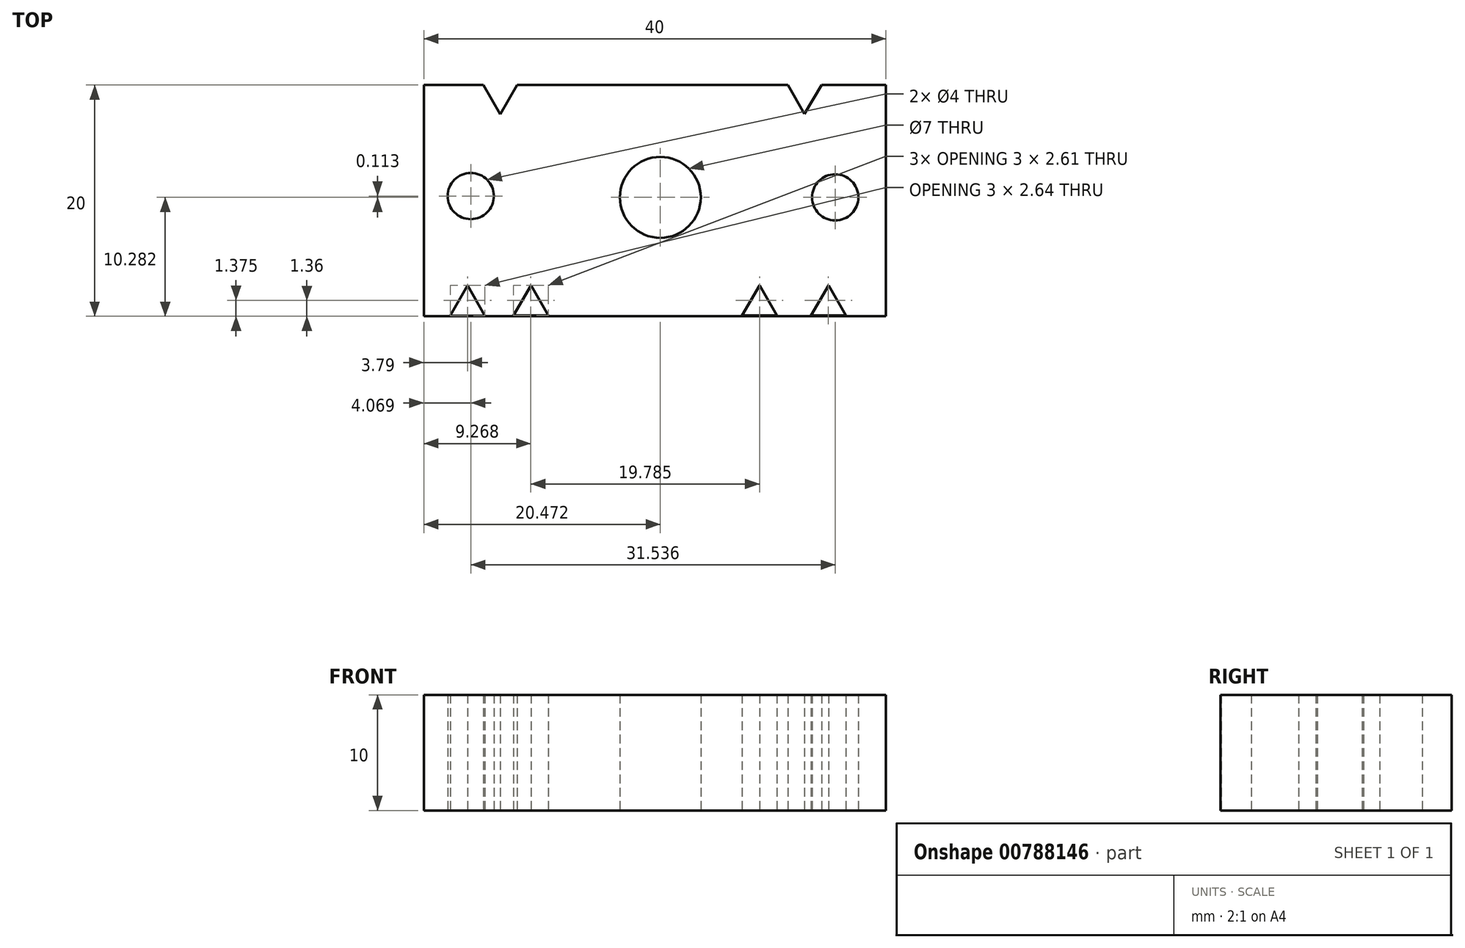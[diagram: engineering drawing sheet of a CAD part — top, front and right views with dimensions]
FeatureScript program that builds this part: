
annotation { "Feature Type Name" : "Feature", "Feature Type Description" : "" }
export const myFeature = defineFeature(function(context is Context, id is Id, definition is map)
    precondition{}
    {
        {
            var Q0;
            Q0=qCreatedBy(makeId("Top.planeOp"),FACE);
            var sketch = newSketch(context, id + "F0", { "sketchPlane" : qUnion([Q0])});
            skLineSegment(sketch, "E0.bottom", {"start": v(-22.8, 21.37) * mm, "end": v(17.2, 21.37) * mm});
            skLineSegment(sketch, "E0.top", {"start": v(-22.8, 1.37) * mm, "end": v(17.2, 1.37) * mm});
            skLineSegment(sketch, "E0.left", {"start": v(-22.8, 21.37) * mm, "end": v(-22.8, 1.37) * mm});
            skLineSegment(sketch, "E0.right", {"start": v(17.2, 21.37) * mm, "end": v(17.2, 1.37) * mm});
            skSolve(sketch);
        }
        {
            var Q0;
            Q0=makeQuery(id+"F0.imprint","IMPRINT",FACE,{"disambiguationData":[TD([[makeQuery(id+"F0.imprint","IMPRINT",EDGE,{"derivedFrom":sQuery(id+"F0.wireOp",EDGE,"E0.bottom")}),-1.0]])]});
            var sketch = newSketch(context, id + "F1", { "sketchPlane" : qUnion([Q0])});
            skLineSegment(sketch, "E1", {"start": v(-20.5, 1.44) * mm, "end": v(-19, 4.05) * mm});
            skLineSegment(sketch, "E2", {"start": v(-19, 4.05) * mm, "end": v(-17.5, 1.4) * mm});
            skLineSegment(sketch, "E3", {"start": v(-17.5, 1.4) * mm, "end": v(-20.5, 1.44) * mm});
            skLineSegment(sketch, "E4", {"start": v(-15.03, 1.44) * mm, "end": v(-13.5, 4.05) * mm});
            skLineSegment(sketch, "E5", {"start": v(-13.5, 4.05) * mm, "end": v(-12.03, 1.44) * mm});
            skLineSegment(sketch, "E6", {"start": v(-12.03, 1.44) * mm, "end": v(-15.03, 1.44) * mm});
            skLineSegment(sketch, "E7", {"start": v(4.75, 1.44) * mm, "end": v(6.28, 4.05) * mm});
            skLineSegment(sketch, "E8", {"start": v(6.28, 4.05) * mm, "end": v(7.75, 1.44) * mm});
            skLineSegment(sketch, "E9", {"start": v(7.75, 1.44) * mm, "end": v(4.75, 1.44) * mm});
            skLineSegment(sketch, "E10", {"start": v(10.72, 1.44) * mm, "end": v(12.24, 4.05) * mm});
            skLineSegment(sketch, "E11", {"start": v(12.24, 4.05) * mm, "end": v(13.72, 1.44) * mm});
            skLineSegment(sketch, "E12", {"start": v(13.72, 1.44) * mm, "end": v(10.72, 1.44) * mm});
            skLineSegment(sketch, "E13", {"start": v(-14.68, 21.44) * mm, "end": v(-17.68, 21.44) * mm});
            skLineSegment(sketch, "E14", {"start": v(-17.68, 21.44) * mm, "end": v(-16.18, 18.84) * mm});
            skLineSegment(sketch, "E15", {"start": v(-16.18, 18.84) * mm, "end": v(-14.68, 21.44) * mm});
            skLineSegment(sketch, "E16", {"start": v(11.65, 21.44) * mm, "end": v(8.65, 21.47) * mm});
            skLineSegment(sketch, "E17", {"start": v(8.65, 21.47) * mm, "end": v(10.13, 18.85) * mm});
            skLineSegment(sketch, "E18", {"start": v(10.13, 18.85) * mm, "end": v(11.65, 21.44) * mm});
            skCircle(sketch, "E19", {"center": v(-18.73, 11.76) * mm, "radius": 2 * mm});
            skCircle(sketch, "E20", {"center": v(12.8, 11.65) * mm, "radius": 2 * mm});
            skCircle(sketch, "E21", {"center": v(-2.33, 11.65) * mm, "radius": 3.5 * mm});
            skSolve(sketch);
        }
        {
            var Q0;
            Q0=makeQuery(id+"F0.imprint","IMPRINT",FACE,{"disambiguationData":[TD([[makeQuery(id+"F0.imprint","IMPRINT",EDGE,{"derivedFrom":sQuery(id+"F0.wireOp",EDGE,"E0.bottom")}),-1.0]])]});
            extrude(context, id + "F2", {"entities" : qUnion([Q0]), "depth" : 10 * mm, "offsetDistance" : 25 * mm});
        }
        {
            var Q0;
            Q0=makeQuery(id+"F1.imprint","IMPRINT",FACE,{"disambiguationData":[TD([[makeQuery(id+"F1.imprint","IMPRINT",EDGE,{"derivedFrom":sQuery(id+"F1.wireOp",EDGE,"E1")}),-1.0]])]});
            var Q1;
            Q1=makeQuery(id+"F1.imprint","IMPRINT",FACE,{"disambiguationData":[TD([[makeQuery(id+"F1.imprint","IMPRINT",EDGE,{"derivedFrom":sQuery(id+"F1.wireOp",EDGE,"E4")}),-1.0]])]});
            var Q2;
            Q2=makeQuery(id+"F1.imprint","IMPRINT",FACE,{"disambiguationData":[TD([[makeQuery(id+"F1.imprint","IMPRINT",EDGE,{"derivedFrom":sQuery(id+"F1.wireOp",EDGE,"E7")}),-1.0]])]});
            var Q3;
            Q3=makeQuery(id+"F1.imprint","IMPRINT",FACE,{"disambiguationData":[TD([[makeQuery(id+"F1.imprint","IMPRINT",EDGE,{"derivedFrom":sQuery(id+"F1.wireOp",EDGE,"E10")}),-1.0]])]});
            var Q4;
            Q4=makeQuery(id+"F1.imprint","IMPRINT",FACE,{"disambiguationData":[TD([[makeQuery(id+"F1.imprint","IMPRINT",EDGE,{"derivedFrom":sQuery(id+"F1.wireOp",EDGE,"E20")}),1.0]])]});
            var Q5;
            Q5=makeQuery(id+"F1.imprint","IMPRINT",FACE,{"disambiguationData":[TD([[makeQuery(id+"F1.imprint","IMPRINT",EDGE,{"derivedFrom":sQuery(id+"F1.wireOp",EDGE,"E21")}),1.0]])]});
            var Q6;
            Q6=makeQuery(id+"F1.imprint","IMPRINT",FACE,{"disambiguationData":[TD([[makeQuery(id+"F1.imprint","IMPRINT",EDGE,{"derivedFrom":sQuery(id+"F1.wireOp",EDGE,"E19")}),1.0]])]});
            var Q7;
            {var subQ0=sQuery(id+"F1.wireOp",EDGE,"E15");var subQ1=sQuery(id+"F1.wireOp",EDGE,"E14");var subQ2=makeQuery(id+"F1.imprint","INTERSECT",VERTEX,{"derivedFrom":[subQ1,subQ0]});Q7=makeQuery(id+"F1.imprint","IMPRINT",FACE,{"disambiguationData":[TD([[makeQuery(id+"F1.imprint","IMPRINT",EDGE,{"disambiguationData":[TD([[subQ2,1.0]])],"derivedFrom":subQ1}),1.0]])]});}
            var Q8;
            {var subQ0=sQuery(id+"F1.wireOp",EDGE,"E18");var subQ1=sQuery(id+"F1.wireOp",EDGE,"E17");var subQ2=makeQuery(id+"F1.imprint","INTERSECT",VERTEX,{"derivedFrom":[subQ1,subQ0]});Q8=makeQuery(id+"F1.imprint","IMPRINT",FACE,{"disambiguationData":[TD([[makeQuery(id+"F1.imprint","IMPRINT",EDGE,{"disambiguationData":[TD([[subQ2,1.0]])],"derivedFrom":subQ1}),1.0]])]});}
            extrude(context, id + "F3", {"entities" : qUnion([Q0, Q1, Q2, Q3, Q4, Q5, Q6, Q7, Q8]), "operationType" : NewBodyOperationType.REMOVE, "endBound" : BoundingType.THROUGH_ALL, "depth" : 25 * mm, "offsetDistance" : 25 * mm});
        }
    });
